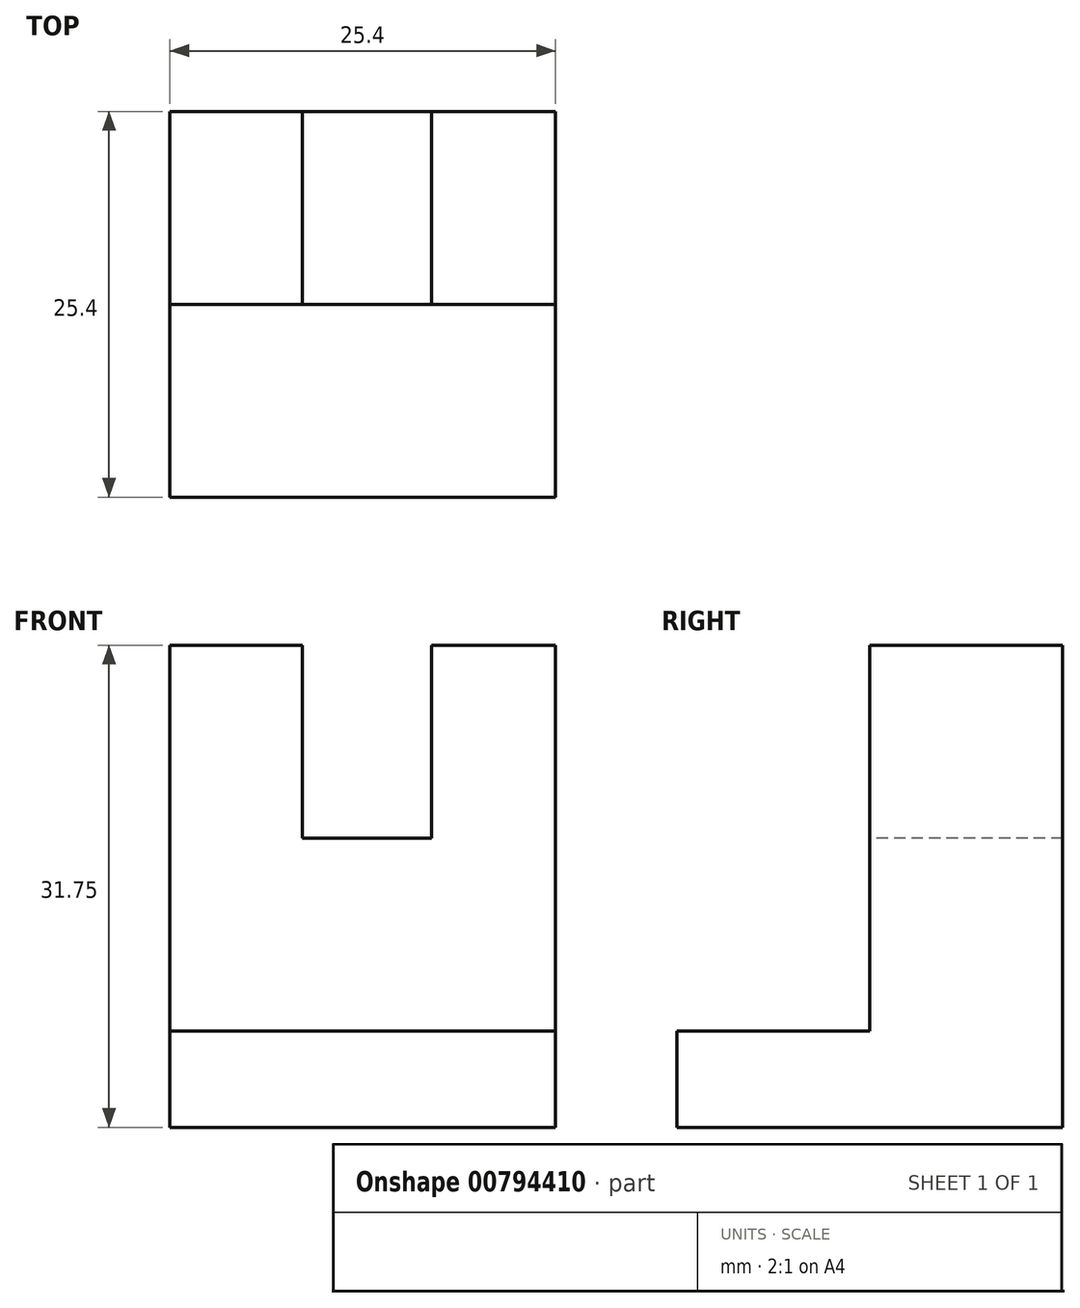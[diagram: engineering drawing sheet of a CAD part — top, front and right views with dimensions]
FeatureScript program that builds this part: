
annotation { "Feature Type Name" : "Feature", "Feature Type Description" : "" }
export const myFeature = defineFeature(function(context is Context, id is Id, definition is map)
    precondition{}
    {
        {
            var Q0;
            Q0=qCreatedBy(makeId("Right.planeOp"),FACE);
            var sketch = newSketch(context, id + "F0", { "sketchPlane" : qUnion([Q0])});
            skLineSegment(sketch, "E0", {"start": v(25.4, 0) * mm, "end": v(0, 0) * mm});
            skLineSegment(sketch, "E1", {"start": v(25.4, 31.75) * mm, "end": v(25.4, 0) * mm});
            skLineSegment(sketch, "E2", {"start": v(12.7, 31.75) * mm, "end": v(25.4, 31.75) * mm});
            skLineSegment(sketch, "E3", {"start": v(12.7, 6.35) * mm, "end": v(12.7, 31.75) * mm});
            skLineSegment(sketch, "E4", {"start": v(0, 6.35) * mm, "end": v(0, 0) * mm});
            skLineSegment(sketch, "E5", {"start": v(12.7, 6.35) * mm, "end": v(0, 6.35) * mm});
            skSolve(sketch);
        }
        {
            var Q0;
            Q0=makeQuery(id+"F0.imprint","IMPRINT",FACE,{"disambiguationData":[TD([[makeQuery(id+"F0.imprint","IMPRINT",EDGE,{"derivedFrom":sQuery(id+"F0.wireOp",EDGE,"E0")}),-1.0]])]});
            extrude(context, id + "F1", {"entities" : qUnion([Q0]), "depth" : 25.4 * mm, "offsetDistance" : 25.4 * mm});
        }
        {
            var Q0;
            Q0=makeQuery(id+"F1.opExtrude","SWEPT_FACE",FACE,{"disambiguationData":[OSD([sQuery(id+"F0.wireOp",EDGE,"E2")])]});
            var sketch = newSketch(context, id + "F2", { "sketchPlane" : qUnion([Q0])});
            skLineSegment(sketch, "E6", {"start": v(8.73, 25.4) * mm, "end": v(8.73, 12.7) * mm});
            skPoint(sketch, "E6.endSnap0", {"position": v(12.7, 12.7) * mm});
            skLineSegment(sketch, "E7", {"start": v(8.73, 12.7) * mm, "end": v(17.23, 12.7) * mm});
            skLineSegment(sketch, "E8", {"start": v(17.23, 12.7) * mm, "end": v(17.23, 25.4) * mm});
            skLineSegment(sketch, "E9", {"start": v(17.23, 25.4) * mm, "end": v(8.73, 25.4) * mm});
            skSolve(sketch);
        }
        {
            var Q0;
            Q0=makeQuery(id+"F2.imprint","IMPRINT",FACE,{"disambiguationData":[TD([[makeQuery(id+"F2.imprint","IMPRINT",EDGE,{"derivedFrom":sQuery(id+"F2.wireOp",EDGE,"E6")}),1.0]])]});
            extrude(context, id + "F3", {"entities" : qUnion([Q0]), "operationType" : NewBodyOperationType.REMOVE, "endBound" : BoundingType.SYMMETRIC, "oppositeDirection" : true, "depth" : 25.4 * mm, "offsetDistance" : 25.4 * mm});
        }
    });
